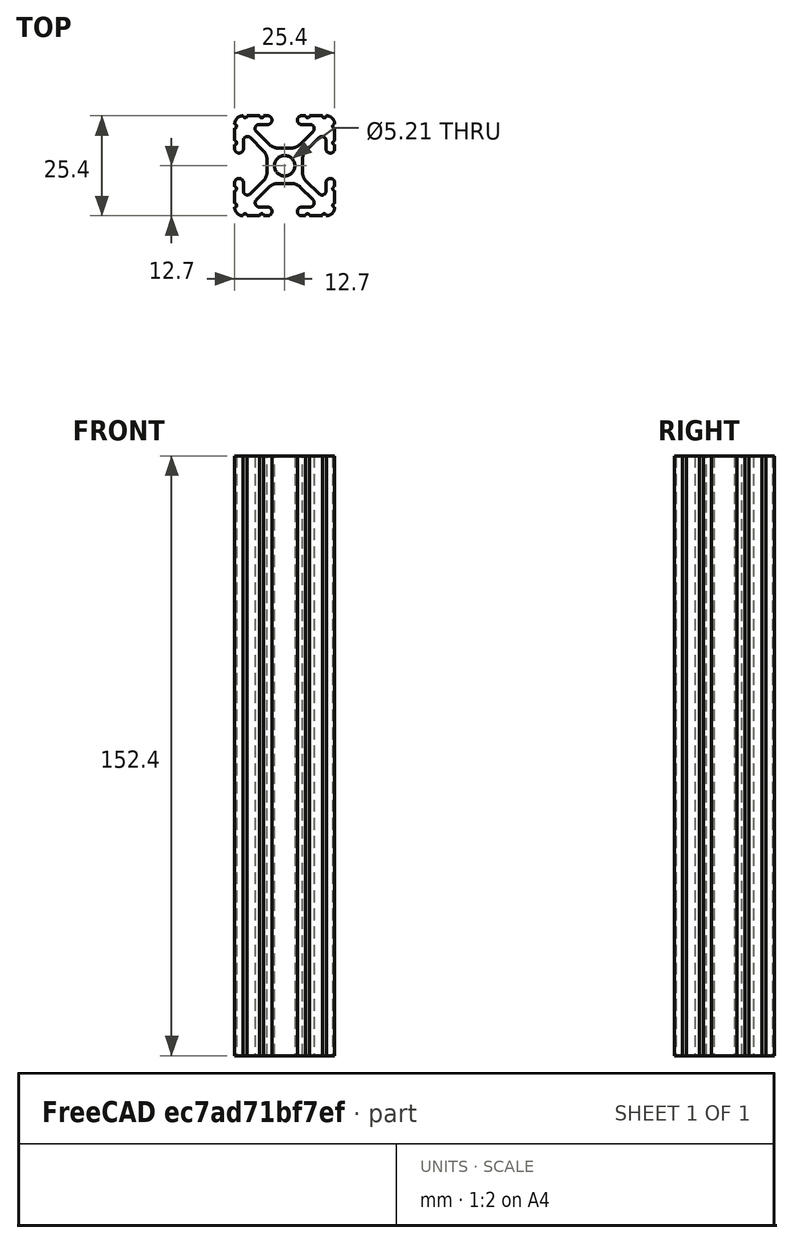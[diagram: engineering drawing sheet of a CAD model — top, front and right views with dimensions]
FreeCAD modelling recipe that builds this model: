
FCSTD DOCUMENT  (FreeCAD 0.19R24267 (Git))
Label: 1010-6
License: All rights reserved
LicenseURL: http://en.wikipedia.org/wiki/All_rights_reserved
objects: Sketcher::SketchObject×1, Part::Extrusion×1
note: 2 computed .brp shape members not serialized (recipe doc carries the construction recipe); baked Part::Feature solids carry a one-line shape summary decoded from their .brp

FEATURE [Sketcher::SketchObject] Sketch097
  FullyConstrained = false
  sketch-geometry (97):
    g0: Circle CenterX=0 CenterY=0 CenterZ=0 NormalX=0 NormalY=0 NormalZ=-1 AngleXU=0 Radius=2.6035
    g1: ArcOfCircle CenterX=12.7 CenterY=5.82508 CenterZ=0 NormalX=0 NormalY=0 NormalZ=1 AngleXU=0 Radius=0.508 StartAngle=1.5708 EndAngle=4.71239
    g2: LineSegment StartX=3.2385 StartY=11.651 StartZ=0 EndX=3.2385 EndY=11.5392 EndZ=0
    g3: LineSegment StartX=6.33313 StartY=-12.7 StartZ=0 EndX=9.55044 EndY=-12.7 EndZ=0
    g4: LineSegment StartX=7.20704 StartY=8.72437 StartZ=0 EndX=3.89827 EndY=5.42317 EndZ=0
    g5: ArcOfCircle CenterX=7.6835 CenterY=1.59319 CenterZ=0 NormalX=0 NormalY=0 NormalZ=1 AngleXU=0 Radius=3.175 StartAngle=2.35505 EndAngle=3.14159
    g6: ArcOfCircle CenterX=-1.70925 CenterY=-7.6708 CenterZ=0 NormalX=0 NormalY=0 NormalZ=1 AngleXU=0 Radius=3.175 StartAngle=1.5708 EndAngle=2.35528
    g7: ArcOfCircle CenterX=11.5392 CenterY=-4.28747 CenterZ=0 NormalX=0 NormalY=0 NormalZ=1 AngleXU=0 Radius=1.04901 StartAngle=1.5708 EndAngle=3.14159
    g8: ArcOfCircle CenterX=12.7 CenterY=-5.82508 CenterZ=0 NormalX=0 NormalY=0 NormalZ=1 AngleXU=0 Radius=0.508 StartAngle=1.5708 EndAngle=4.71239
    g9: LineSegment StartX=4.28751 StartY=10.4902 StartZ=0 EndX=6.47679 EndY=10.4902 EndZ=0
    g10: ArcOfCircle CenterX=4.28751 CenterY=11.651 CenterZ=0 NormalX=0 NormalY=0 NormalZ=1 AngleXU=0 Radius=1.04901 StartAngle=1.5708 EndAngle=3.14159
    g11: ArcOfCircle CenterX=6.47679 CenterY=9.45629 CenterZ=0 NormalX=0 NormalY=0 NormalZ=1 AngleXU=0 Radius=1.03391 StartAngle=5.49664 EndAngle=7.85398
    g12: ArcOfCircle CenterX=4.28751 CenterY=11.5392 CenterZ=0 NormalX=0 NormalY=0 NormalZ=1 AngleXU=0 Radius=1.04901 StartAngle=3.14159 EndAngle=4.71239
    g13: LineSegment StartX=3.95227 StartY=-5.42369 StartZ=0 EndX=7.17965 EndY=-8.64519 EndZ=0
    g14: ArcOfCircle CenterX=11.651 CenterY=4.28747 CenterZ=0 NormalX=0 NormalY=0 NormalZ=1 AngleXU=0 Radius=1.04901 StartAngle=4.71239 EndAngle=6.28319
    g15: ArcOfCircle CenterX=-5.82513 CenterY=-12.7 CenterZ=0 NormalX=0 NormalY=0 NormalZ=1 AngleXU=0 Radius=0.508 StartAngle=0 EndAngle=3.14159
    g16: LineSegment StartX=-6.47679 StartY=10.4902 StartZ=0 EndX=-4.28751 EndY=10.4902 EndZ=0
    g17: ArcOfCircle CenterX=-12.7 CenterY=10.0584 CenterZ=0 NormalX=0 NormalY=0 NormalZ=1 AngleXU=0 Radius=0.508 StartAngle=4.71239 EndAngle=7.85368
    g18: ArcOfCircle CenterX=-12.7 CenterY=5.82508 CenterZ=0 NormalX=0 NormalY=0 NormalZ=1 AngleXU=0 Radius=0.508 StartAngle=4.71239 EndAngle=7.85398
    g19: LineSegment StartX=-11.5392 StartY=-3.23846 StartZ=0 EndX=-11.651 EndY=-3.23846 EndZ=0
    g20: LineSegment StartX=-3.89827 StartY=5.42317 StartZ=0 EndX=-7.20704 EndY=8.72437 EndZ=0
    g21: LineSegment StartX=1.65578 StartY=4.4958 StartZ=0 EndX=-1.65578 EndY=4.4958 EndZ=0
    g22: ArcOfCircle CenterX=-1.65578 CenterY=7.6708 CenterZ=0 NormalX=0 NormalY=0 NormalZ=1 AngleXU=0 Radius=3.175 StartAngle=3.92813 EndAngle=4.71239
    g23: LineSegment StartX=-9.55044 StartY=-12.7 StartZ=0 EndX=-6.33313 EndY=-12.7 EndZ=0
    g24: ArcOfCircle CenterX=-5.82513 CenterY=12.7 CenterZ=0 NormalX=0 NormalY=0 NormalZ=1 AngleXU=0 Radius=0.508 StartAngle=3.14159 EndAngle=6.28319
    g25: ArcOfCircle CenterX=-4.28751 CenterY=11.651 CenterZ=0 NormalX=0 NormalY=0 NormalZ=1 AngleXU=0 Radius=1.04901 StartAngle=0 EndAngle=1.5708
    g26: LineSegment StartX=-12.7 StartY=-4.28747 StartZ=0 EndX=-12.7 EndY=-5.31708 EndZ=0
    g27: ArcOfCircle CenterX=-6.47679 CenterY=9.45629 CenterZ=0 NormalX=0 NormalY=0 NormalZ=1 AngleXU=0 Radius=1.03391 StartAngle=1.5708 EndAngle=3.92813
    g28: ArcOfCircle CenterX=-4.28751 CenterY=11.5392 CenterZ=0 NormalX=0 NormalY=0 NormalZ=1 AngleXU=0 Radius=1.04901 StartAngle=4.71239 EndAngle=6.28319
    g29: LineSegment StartX=-5.44101 StartY=-3.84082 StartZ=0 EndX=-8.73713 EndY=-7.12941 EndZ=0
    g30: ArcOfCircle CenterX=-7.6835 CenterY=-1.59319 CenterZ=0 NormalX=0 NormalY=0 NormalZ=1 AngleXU=0 Radius=3.175 StartAngle=5.49664 EndAngle=6.28319
    g31: LineSegment StartX=-12.7 StartY=5.31708 StartZ=0 EndX=-12.7 EndY=4.28747 EndZ=0
    g32: LineSegment StartX=-8.73713 StartY=7.12941 StartZ=0 EndX=-5.44101 EndY=3.84082 EndZ=0
    g33: LineSegment StartX=-11.651 StartY=3.23846 StartZ=0 EndX=-11.5392 EndY=3.23846 EndZ=0
    g34: ArcOfCircle CenterX=-9.46279 CenterY=-6.40209 CenterZ=0 NormalX=0 NormalY=0 NormalZ=1 AngleXU=0 Radius=1.02741 StartAngle=3.14159 EndAngle=5.49664
    g35: ArcOfCircle CenterX=-10.5918 CenterY=10.5918 CenterZ=0 NormalX=0 NormalY=0 NormalZ=1 AngleXU=0 Radius=2.1082 StartAngle=1.55877 EndAngle=3.15364
    g36: LineSegment StartX=-12.7 StartY=9.5504 StartZ=0 EndX=-12.7 EndY=6.33308 EndZ=0
    g37: LineSegment StartX=-6.33313 StartY=12.7 StartZ=0 EndX=-9.55044 EndY=12.7 EndZ=0
    g38: ArcOfCircle CenterX=-11.5392 CenterY=-4.28747 CenterZ=0 NormalX=0 NormalY=0 NormalZ=1 AngleXU=0 Radius=1.04901 StartAngle=0 EndAngle=1.5708
    g39: LineSegment StartX=4.28751 StartY=-12.7 StartZ=0 EndX=5.31713 EndY=-12.7 EndZ=0
    g40: LineSegment StartX=5.44101 StartY=3.84082 StartZ=0 EndX=8.73713 EndY=7.12941 EndZ=0
    g41: LineSegment StartX=10.4902 StartY=-4.28747 StartZ=0 EndX=10.4902 EndY=-6.40209 EndZ=0
    g42: ArcOfCircle CenterX=9.46279 CenterY=6.40209 CenterZ=0 NormalX=0 NormalY=0 NormalZ=1 AngleXU=0 Radius=1.02741 StartAngle=0 EndAngle=2.35505
    g43: ArcOfCircle CenterX=5.82513 CenterY=-12.7 CenterZ=0 NormalX=0 NormalY=0 NormalZ=1 AngleXU=0 Radius=0.508 StartAngle=0 EndAngle=3.14159
    g44: LineSegment StartX=12.7 StartY=-9.5504 StartZ=0 EndX=12.7 EndY=-6.33308 EndZ=0
    g45: LineSegment StartX=4.5085 StartY=-1.59319 StartZ=0 EndX=4.5085 EndY=1.59319 EndZ=0
    g46: ArcOfCircle CenterX=12.7 CenterY=10.0584 CenterZ=0 NormalX=0 NormalY=0 NormalZ=1 AngleXU=0 Radius=0.508 StartAngle=1.5711 EndAngle=4.71239
    g47: ArcOfCircle CenterX=12.7 CenterY=-10.0584 CenterZ=0 NormalX=0 NormalY=0 NormalZ=1 AngleXU=0 Radius=0.508 StartAngle=1.5708 EndAngle=4.71209
    g48: LineSegment StartX=3.2385 StartY=-11.5392 StartZ=0 EndX=3.2385 EndY=-11.651 EndZ=0
    g49: LineSegment StartX=8.73713 StartY=-7.12941 StartZ=0 EndX=5.44101 EndY=-3.84082 EndZ=0
    g50: ArcOfCircle CenterX=11.651 CenterY=-4.28747 CenterZ=0 NormalX=0 NormalY=0 NormalZ=1 AngleXU=0 Radius=1.04901 StartAngle=0 EndAngle=1.5708
    g51: ArcOfCircle CenterX=1.65578 CenterY=7.6708 CenterZ=0 NormalX=0 NormalY=0 NormalZ=1 AngleXU=0 Radius=3.175 StartAngle=4.71239 EndAngle=5.49664
    g52: ArcOfCircle CenterX=7.6835 CenterY=-1.59319 CenterZ=0 NormalX=0 NormalY=0 NormalZ=1 AngleXU=0 Radius=3.175 StartAngle=3.14159 EndAngle=3.92813
    g53: LineSegment StartX=12.7 StartY=4.28747 StartZ=0 EndX=12.7 EndY=5.31708 EndZ=0
    g54: ArcOfCircle CenterX=6.41641 CenterY=-9.40983 CenterZ=0 NormalX=0 NormalY=0 NormalZ=1 AngleXU=0 Radius=1.08037 StartAngle=4.71239 EndAngle=7.06949
    g55: LineSegment StartX=12.7 StartY=-5.31708 StartZ=0 EndX=12.7 EndY=-4.28747 EndZ=0
    g56: ArcOfCircle CenterX=10.0584 CenterY=-12.7 CenterZ=0 NormalX=0 NormalY=0 NormalZ=1 AngleXU=0 Radius=0.508 StartAngle=0.000300194 EndAngle=3.14159
    g57: ArcOfCircle CenterX=11.5392 CenterY=4.28747 CenterZ=0 NormalX=0 NormalY=0 NormalZ=1 AngleXU=0 Radius=1.04901 StartAngle=3.14159 EndAngle=4.71239
    g58: LineSegment StartX=12.7 StartY=6.33308 StartZ=0 EndX=12.7 EndY=9.5504 EndZ=0
    g59: ArcOfCircle CenterX=4.28751 CenterY=-11.5392 CenterZ=0 NormalX=0 NormalY=0 NormalZ=1 AngleXU=0 Radius=1.04901 StartAngle=1.5708 EndAngle=3.14159
    g60: ArcOfCircle CenterX=10.5918 CenterY=10.5918 CenterZ=0 NormalX=0 NormalY=0 NormalZ=1 AngleXU=0 Radius=2.1082 StartAngle=6.27114 EndAngle=7.86601
    g61: ArcOfCircle CenterX=9.46279 CenterY=-6.40209 CenterZ=0 NormalX=0 NormalY=0 NormalZ=1 AngleXU=0 Radius=1.02741 StartAngle=3.92813 EndAngle=6.28319
    g62: LineSegment StartX=6.41641 StartY=-10.4902 StartZ=0 EndX=4.28751 EndY=-10.4902 EndZ=0
    g63: LineSegment StartX=-10.4902 StartY=-6.40209 StartZ=0 EndX=-10.4902 EndY=-4.28747 EndZ=0
    g64: ArcOfCircle CenterX=-9.46279 CenterY=6.40209 CenterZ=0 NormalX=0 NormalY=0 NormalZ=1 AngleXU=0 Radius=1.02741 StartAngle=0.786542 EndAngle=3.14159
    g65: LineSegment StartX=-10.4902 StartY=4.28747 StartZ=0 EndX=-10.4902 EndY=6.40209 EndZ=0
    g66: LineSegment StartX=-4.5085 StartY=1.59319 StartZ=0 EndX=-4.5085 EndY=-1.59319 EndZ=0
    g67: LineSegment StartX=-4.28751 StartY=12.7 StartZ=0 EndX=-5.31713 EndY=12.7 EndZ=0
    g68: ArcOfCircle CenterX=-11.5392 CenterY=4.28747 CenterZ=0 NormalX=0 NormalY=0 NormalZ=1 AngleXU=0 Radius=1.04901 StartAngle=4.71239 EndAngle=6.28319
    g69: LineSegment StartX=-3.2385 StartY=11.5392 StartZ=0 EndX=-3.2385 EndY=11.651 EndZ=0
    g70: ArcOfCircle CenterX=-11.651 CenterY=4.28747 CenterZ=0 NormalX=0 NormalY=0 NormalZ=1 AngleXU=0 Radius=1.04901 StartAngle=3.14159 EndAngle=4.71239
    g71: ArcOfCircle CenterX=-7.6835 CenterY=1.59319 CenterZ=0 NormalX=0 NormalY=0 NormalZ=1 AngleXU=0 Radius=3.175 StartAngle=0 EndAngle=0.786542
    g72: ArcOfCircle CenterX=-10.0584 CenterY=12.7 CenterZ=0 NormalX=0 NormalY=0 NormalZ=1 AngleXU=0 Radius=0.508 StartAngle=3.14189 EndAngle=6.28319
    g73: LineSegment StartX=-1.70925 StartY=-4.4958 StartZ=0 EndX=1.70925 EndY=-4.4958 EndZ=0
    g74: LineSegment StartX=11.651 StartY=-3.23846 StartZ=0 EndX=11.5392 EndY=-3.23846 EndZ=0
    g75: ArcOfCircle CenterX=-10.5918 CenterY=-10.5918 CenterZ=0 NormalX=0 NormalY=0 NormalZ=1 AngleXU=0 Radius=2.1082 StartAngle=3.12954 EndAngle=4.72442
    g76: ArcOfCircle CenterX=10.5918 CenterY=-10.5918 CenterZ=0 NormalX=0 NormalY=0 NormalZ=1 AngleXU=0 Radius=2.1082 StartAngle=4.70036 EndAngle=6.29523
    g77: ArcOfCircle CenterX=-12.7 CenterY=-5.82508 CenterZ=0 NormalX=0 NormalY=0 NormalZ=1 AngleXU=0 Radius=0.508 StartAngle=4.71239 EndAngle=7.85398
    g78: ArcOfCircle CenterX=5.82513 CenterY=12.7 CenterZ=0 NormalX=0 NormalY=0 NormalZ=1 AngleXU=0 Radius=0.508 StartAngle=3.14159 EndAngle=6.28319
    g79: LineSegment StartX=9.55044 StartY=12.7 StartZ=0 EndX=6.33313 EndY=12.7 EndZ=0
    g80: ArcOfCircle CenterX=10.0584 CenterY=12.7 CenterZ=0 NormalX=0 NormalY=0 NormalZ=1 AngleXU=0 Radius=0.508 StartAngle=3.14159 EndAngle=6.28289
    g81: ArcOfCircle CenterX=1.70925 CenterY=-7.6708 CenterZ=0 NormalX=0 NormalY=0 NormalZ=1 AngleXU=0 Radius=3.175 StartAngle=0.78631 EndAngle=1.5708
    g82: ArcOfCircle CenterX=4.28751 CenterY=-11.651 CenterZ=0 NormalX=0 NormalY=0 NormalZ=1 AngleXU=0 Radius=1.04901 StartAngle=3.14159 EndAngle=4.71239
    g83: LineSegment StartX=5.31713 StartY=12.7 StartZ=0 EndX=4.28751 EndY=12.7 EndZ=0
    g84: LineSegment StartX=10.4902 StartY=6.40209 StartZ=0 EndX=10.4902 EndY=4.28747 EndZ=0
    g85: LineSegment StartX=11.5392 StartY=3.23846 StartZ=0 EndX=11.651 EndY=3.23846 EndZ=0
    g86: ArcOfCircle CenterX=-10.0584 CenterY=-12.7 CenterZ=0 NormalX=0 NormalY=0 NormalZ=1 AngleXU=0 Radius=0.508 StartAngle=0 EndAngle=3.14129
    g87: ArcOfCircle CenterX=-12.7 CenterY=-10.0584 CenterZ=0 NormalX=0 NormalY=0 NormalZ=1 AngleXU=0 Radius=0.508 StartAngle=4.71269 EndAngle=7.85398
    g88: ArcOfCircle CenterX=-4.28751 CenterY=-11.5392 CenterZ=0 NormalX=0 NormalY=0 NormalZ=1 AngleXU=0 Radius=1.04901 StartAngle=0 EndAngle=1.5708
    g89: ArcOfCircle CenterX=-4.28751 CenterY=-11.651 CenterZ=0 NormalX=0 NormalY=0 NormalZ=1 AngleXU=0 Radius=1.04901 StartAngle=4.71239 EndAngle=6.28319
    g90: LineSegment StartX=-12.7 StartY=-6.33308 StartZ=0 EndX=-12.7 EndY=-9.5504 EndZ=0
    g91: ArcOfCircle CenterX=-11.651 CenterY=-4.28747 CenterZ=0 NormalX=0 NormalY=0 NormalZ=1 AngleXU=0 Radius=1.04901 StartAngle=1.5708 EndAngle=3.14159
    g92: LineSegment StartX=-7.17965 StartY=-8.64519 StartZ=0 EndX=-3.95227 EndY=-5.42369 EndZ=0
    g93: LineSegment StartX=-5.31713 StartY=-12.7 StartZ=0 EndX=-4.28751 EndY=-12.7 EndZ=0
    g94: LineSegment StartX=-3.2385 StartY=-11.651 StartZ=0 EndX=-3.2385 EndY=-11.5392 EndZ=0
    g95: ArcOfCircle CenterX=-6.41641 CenterY=-9.40983 CenterZ=0 NormalX=0 NormalY=0 NormalZ=1 AngleXU=0 Radius=1.08037 StartAngle=2.35528 EndAngle=4.71239
    g96: LineSegment StartX=-4.28751 StartY=-10.4902 StartZ=0 EndX=-6.41641 EndY=-10.4902 EndZ=0
FEATURE [Part::Extrusion] Extrude
  Base = -> Sketch097
  Dir = (0,0,1)
  DirMode = 2
  FaceMakerClass = Part::FaceMakerBullseye
  LengthFwd = 152.4
  LengthRev = 0
  Solid = true
  Symmetric = false
